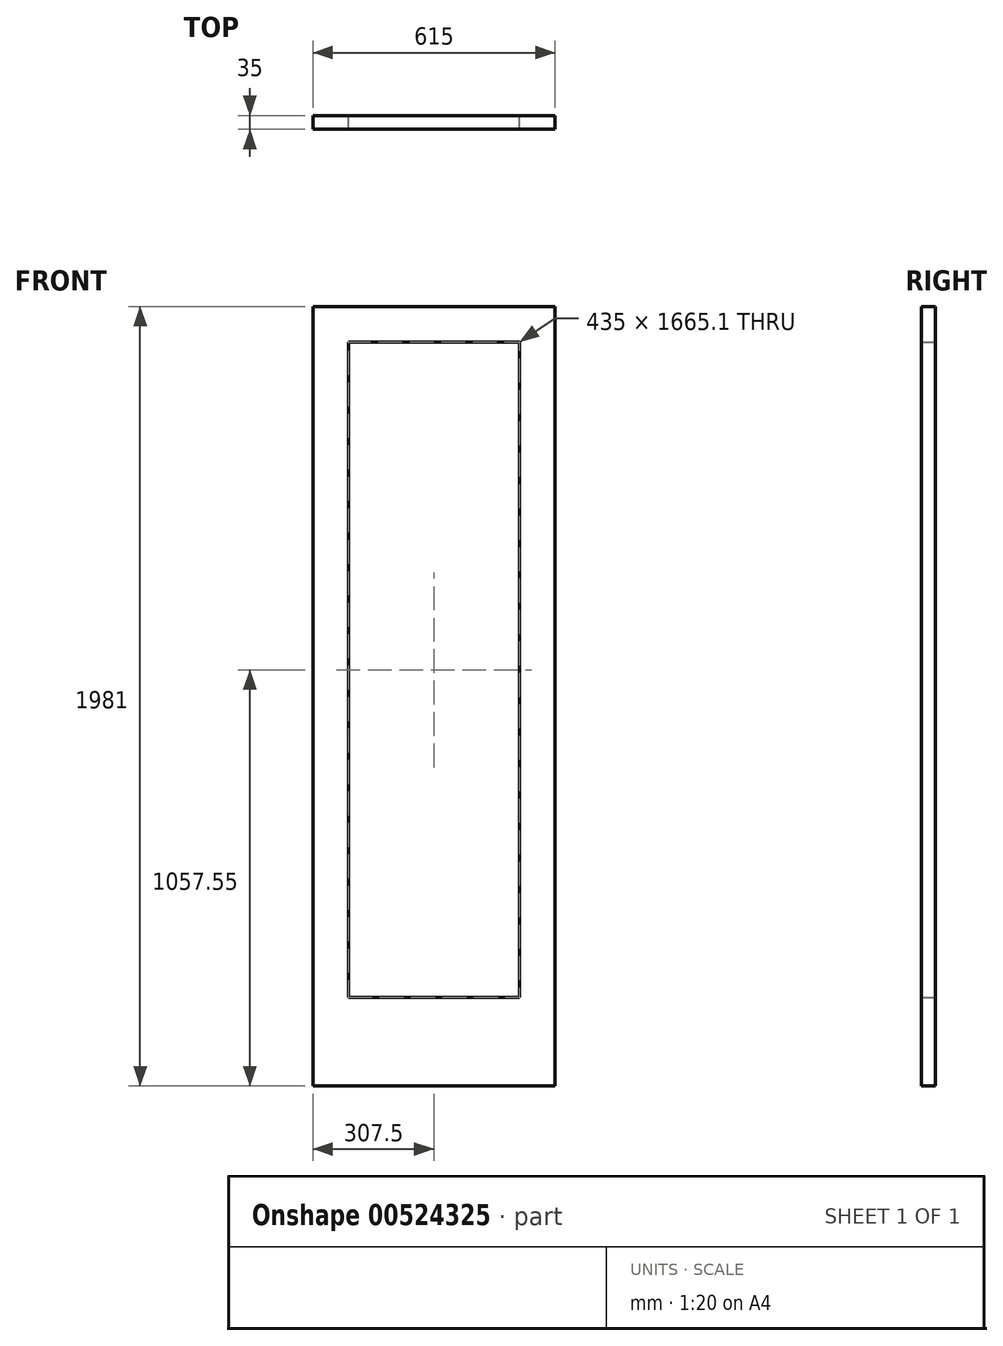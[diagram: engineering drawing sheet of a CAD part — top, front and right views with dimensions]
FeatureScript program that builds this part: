
annotation { "Feature Type Name" : "Feature", "Feature Type Description" : "" }
export const myFeature = defineFeature(function(context is Context, id is Id, definition is map)
    precondition{}
    {
        {
            var Q0;
            Q0=qCreatedBy(makeId("Front.planeOp"),FACE);
            var sketch = newSketch(context, id + "F0", { "sketchPlane" : qUnion([Q0])});
            skLineSegment(sketch, "E0.bottom", {"start": v(0, 0) * mm, "end": v(-615, 0) * mm});
            skLineSegment(sketch, "E0.top", {"start": v(0, 1981) * mm, "end": v(-615, 1981) * mm});
            skLineSegment(sketch, "E0.left", {"start": v(0, 0) * mm, "end": v(0, 1981) * mm});
            skLineSegment(sketch, "E0.right", {"start": v(-615, 0) * mm, "end": v(-615, 1981) * mm});
            skSolve(sketch);
        }
        {
            var Q0;
            Q0=makeQuery(id+"F0.imprint","IMPRINT",FACE,{"disambiguationData":[TD([[makeQuery(id+"F0.imprint","IMPRINT",EDGE,{"derivedFrom":sQuery(id+"F0.wireOp",EDGE,"E0.bottom")}),-1.0]])]});
            extrude(context, id + "F1", {"entities" : qUnion([Q0]), "depth" : 35 * mm, "offsetDistance" : 25 * mm});
        }
        {
            var Q0;
            Q0=makeQuery(id+"F0.imprint","IMPRINT",FACE,{"disambiguationData":[TD([[makeQuery(id+"F0.imprint","IMPRINT",EDGE,{"derivedFrom":sQuery(id+"F0.wireOp",EDGE,"E0.bottom")}),-1.0]])]});
            var sketch = newSketch(context, id + "F2", { "sketchPlane" : qUnion([Q0])});
            skLineSegment(sketch, "E1.0", {"start": v(-90, 225) * mm, "end": v(-90, 1890.1) * mm});
            skLineSegment(sketch, "E1.1", {"start": v(-525, 225) * mm, "end": v(-90, 225) * mm});
            skLineSegment(sketch, "E1.2", {"start": v(-525, 1890.1) * mm, "end": v(-525, 225) * mm});
            skLineSegment(sketch, "E1.3", {"start": v(-90, 1890.1) * mm, "end": v(-525, 1890.1) * mm});
            skSolve(sketch);
        }
        {
            var Q0;
            Q0 = qSketchRegion(id + "F2", true);
            extrude(context, id + "F3", {"entities" : qUnion([Q0]), "operationType" : NewBodyOperationType.REMOVE, "endBound" : BoundingType.THROUGH_ALL, "depth" : 25 * mm, "offsetDistance" : 25 * mm});
        }
    });
